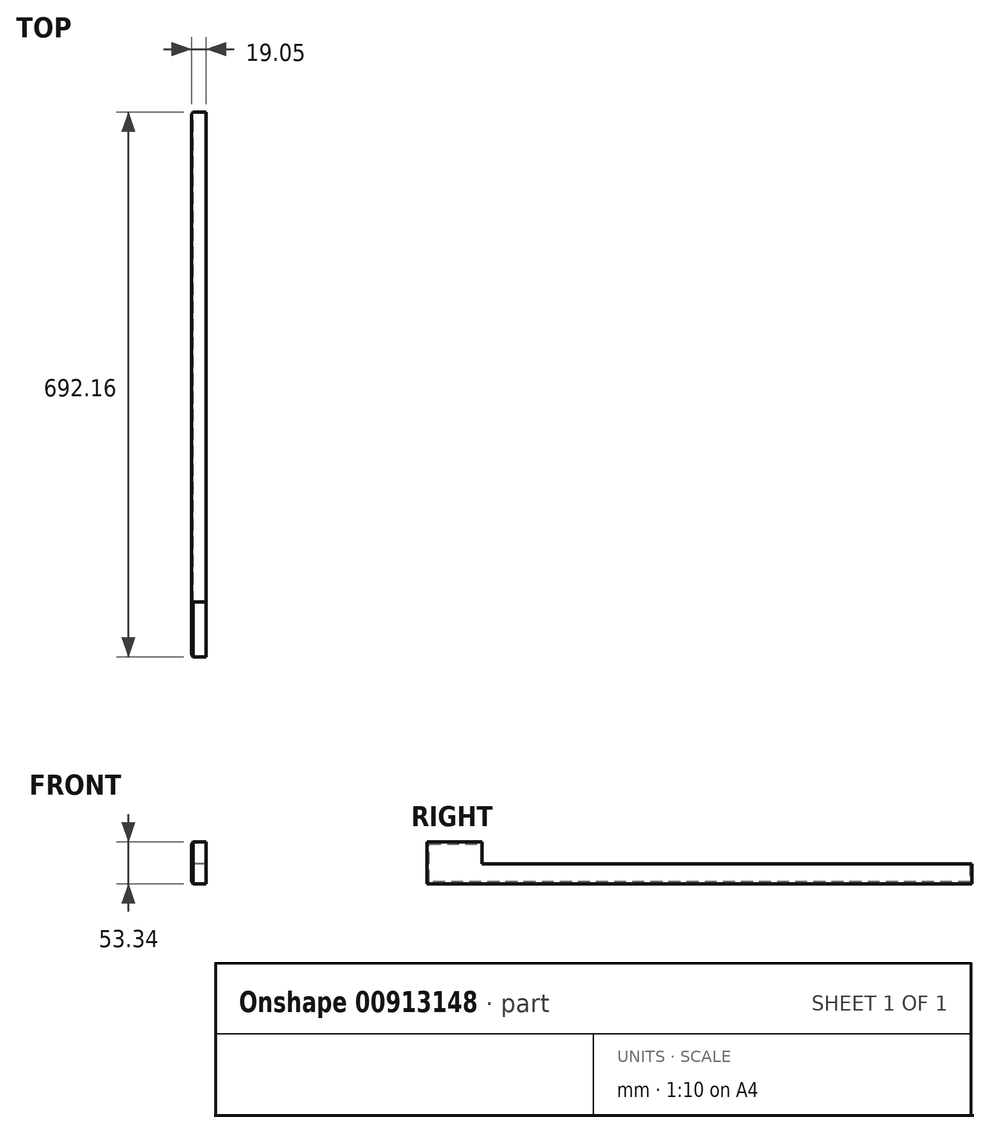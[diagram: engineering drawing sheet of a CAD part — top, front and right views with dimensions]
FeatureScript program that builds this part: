
annotation { "Feature Type Name" : "Feature", "Feature Type Description" : "" }
export const myFeature = defineFeature(function(context is Context, id is Id, definition is map)
    precondition{}
    {
        {
            var Q0;
            Q0=qCreatedBy(makeId("Right.planeOp"),FACE);
            var sketch = newSketch(context, id + "F0", { "sketchPlane" : qUnion([Q0])});
            skLineSegment(sketch, "E0.bottom", {"start": v(-346.08, -26.67) * mm, "end": v(346.08, -26.67) * mm});
            skLineSegment(sketch, "E0.top", {"start": v(-346.08, 26.67) * mm, "end": v(346.08, 26.67) * mm});
            skLineSegment(sketch, "E0.left", {"start": v(-346.08, -26.67) * mm, "end": v(-346.08, 26.67) * mm});
            skLineSegment(sketch, "E0.right", {"start": v(346.08, -26.67) * mm, "end": v(346.08, 26.67) * mm});
            skPoint(sketch, "E0.middle", {"position": v(0, 0) * mm});
            skLineSegment(sketch, "E1.bottom", {"start": v(346.08, 26.67) * mm, "end": v(-276.23, 26.67) * mm});
            skLineSegment(sketch, "E1.top", {"start": v(346.08, -1.27) * mm, "end": v(-276.23, -1.27) * mm});
            skLineSegment(sketch, "E1.left", {"start": v(346.08, 26.67) * mm, "end": v(346.08, -1.27) * mm});
            skLineSegment(sketch, "E1.right", {"start": v(-276.23, 26.67) * mm, "end": v(-276.23, -1.27) * mm});
            skSolve(sketch);
        }
        {
            var Q0;
            Q0=makeQuery(id+"F0.imprint","IMPRINT",FACE,{"disambiguationData":[TD([[makeQuery(id+"F0.imprint","IMPRINT",EDGE,{"derivedFrom":sQuery(id+"F0.wireOp",EDGE,"E0.bottom")}),1.0]])]});
            extrude(context, id + "F1", {"entities" : qUnion([Q0]), "depth" : 19.05 * mm, "offsetDistance" : 25.4 * mm});
        }
        {
            var Q0;
            Q0=makeQuery(id+"F1.opExtrude","CAP_EDGE",EDGE,{"disambiguationData":[OSD([sQuery(id+"F0.wireOp",EDGE,"E0.top")])],"isStart":true});
            var Q1;
            Q1=makeQuery(id+"F1.opExtrude","CAP_EDGE",EDGE,{"disambiguationData":[OSD([sQuery(id+"F0.wireOp",EDGE,"E0.left")])],"isStart":true});
            var Q2;
            Q2=makeQuery(id+"F1.opExtrude","CAP_EDGE",EDGE,{"disambiguationData":[OSD([sQuery(id+"F0.wireOp",EDGE,"E0.bottom")])],"isStart":true});
            var Q3;
            Q3=makeQuery(id+"F1.opExtrude","CAP_EDGE",EDGE,{"disambiguationData":[OSD([sQuery(id+"F0.wireOp",EDGE,"E0.right")])],"isStart":true});
            chamfer(context, id + "F2", {"entities" : qUnion([Q0, Q1, Q2, Q3]), "width" : 2.54 * mm, "tangentPropagation" : true});
        }
    });
